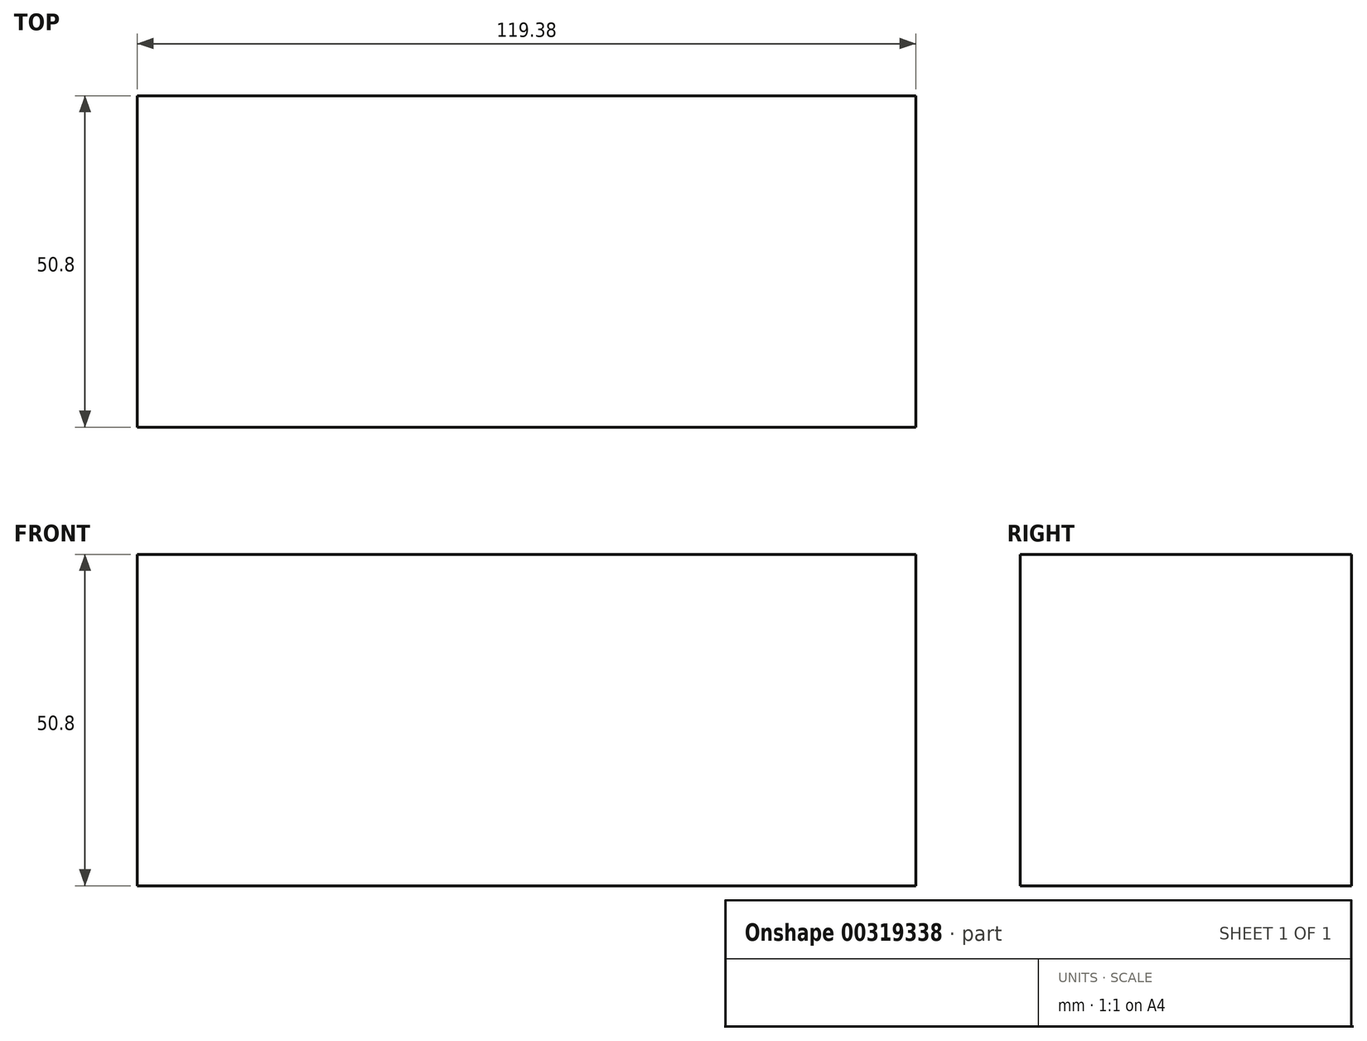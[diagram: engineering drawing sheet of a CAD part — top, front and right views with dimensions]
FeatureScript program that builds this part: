
annotation { "Feature Type Name" : "Feature", "Feature Type Description" : "" }
export const myFeature = defineFeature(function(context is Context, id is Id, definition is map)
    precondition{}
    {
        {
            var Q0;
            Q0=qCreatedBy(makeId("Front.planeOp"),FACE);
            var sketch = newSketch(context, id + "F0", { "sketchPlane" : qUnion([Q0])});
            skLineSegment(sketch, "E0", {"start": v(-67.6, 21.06) * mm, "end": v(-67.6, -29.74) * mm});
            skLineSegment(sketch, "E1", {"start": v(-67.6, 21.06) * mm, "end": v(51.79, 21.06) * mm});
            skLineSegment(sketch, "E2", {"start": v(-67.6, -29.74) * mm, "end": v(51.79, -29.74) * mm});
            skLineSegment(sketch, "E3", {"start": v(51.79, 21.06) * mm, "end": v(51.79, -29.74) * mm});
            skSolve(sketch);
        }
        {
            var Q0;
            Q0 = qSketchRegion(id + "F0", true);
            extrude(context, id + "F1", {"entities" : qUnion([Q0]), "endBound" : BoundingType.SYMMETRIC, "depth" : 50.8 * mm});
        }
        {
            var Q0;
            Q0=makeQuery(id+"F1.opExtrude","CAP_FACE",FACE,{"disambiguationData":[OSD([sQuery(id+"F0.wireOp",EDGE,"E0"),sQuery(id+"F0.wireOp",EDGE,"E1"),sQuery(id+"F0.wireOp",EDGE,"E2"),sQuery(id+"F0.wireOp",EDGE,"E3")])],"isStart":false});
            var sketch = newSketch(context, id + "F2", { "sketchPlane" : qUnion([Q0])});
            skLineSegment(sketch, "E4", {"start": v(-67.6, 21.06) * mm, "end": v(-62.51, 21.06) * mm});
            skLineSegment(sketch, "E5", {"start": v(-67.6, 21.06) * mm, "end": v(-67.6, 15.98) * mm});
            skLineSegment(sketch, "E6", {"start": v(-62.51, 15.98) * mm, "end": v(-62.51, -25.13) * mm});
            skLineSegment(sketch, "E7", {"start": v(51.79, 21.06) * mm, "end": v(46.7, 21.06) * mm});
            skLineSegment(sketch, "E8", {"start": v(51.79, 21.06) * mm, "end": v(51.79, 15.98) * mm});
            skLineSegment(sketch, "E9", {"start": v(-62.51, 15.98) * mm, "end": v(46.7, 15.98) * mm});
            skLineSegment(sketch, "E10", {"start": v(46.7, 15.98) * mm, "end": v(46.7, -25.13) * mm});
            skLineSegment(sketch, "E11", {"start": v(46.7, -25.13) * mm, "end": v(-62.51, -25.13) * mm});
            skSolve(sketch);
        }
        {
            var Q0;
            Q0=makeQuery(id+"F2.imprint","IMPRINT",FACE,{"disambiguationData":[TD([[makeQuery(id+"F2.imprint","IMPRINT",EDGE,{"derivedFrom":sQuery(id+"F2.wireOp",EDGE,"E6")}),1.0]])]});
            extrude(context, id + "F3", {"entities" : qUnion([Q0]), "operationType" : NewBodyOperationType.ADD, "oppositeDirection" : true, "depth" : 25.4 * mm});
        }
    });
